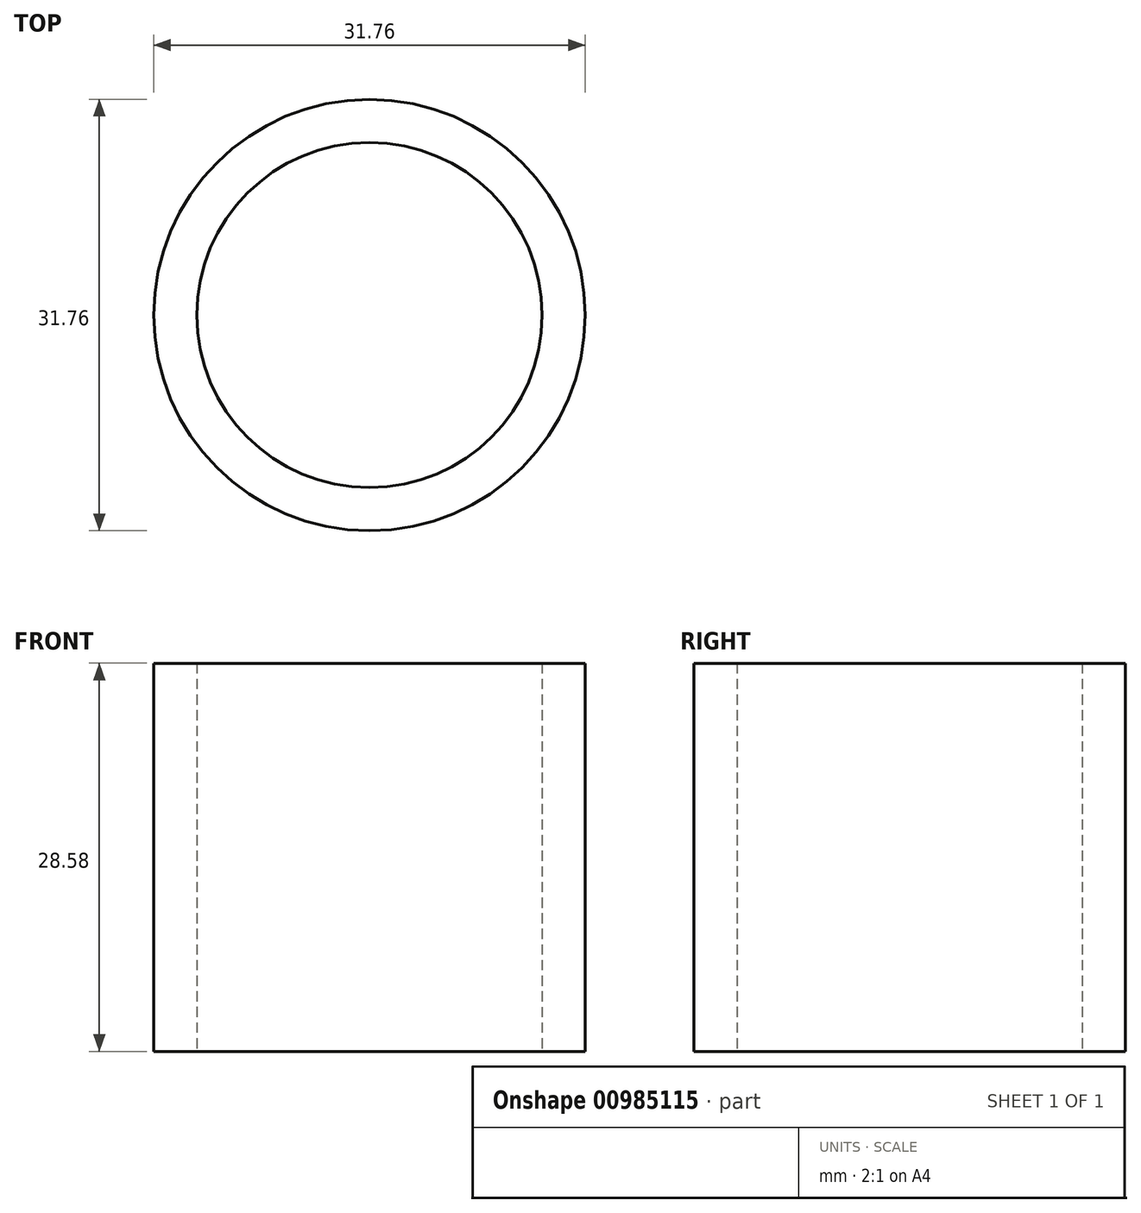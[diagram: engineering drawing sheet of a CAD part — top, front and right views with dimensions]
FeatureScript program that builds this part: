
annotation { "Feature Type Name" : "Feature", "Feature Type Description" : "" }
export const myFeature = defineFeature(function(context is Context, id is Id, definition is map)
    precondition{}
    {
        {
            var Q0;
            Q0=qCreatedBy(makeId("Top.planeOp"),FACE);
            var sketch = newSketch(context, id + "F0", { "sketchPlane" : qUnion([Q0])});
            skCircle(sketch, "E0", {"center": v(0, 0) * mm, "radius": 12.7 * mm});
            skCircle(sketch, "E1.0", {"center": v(0, 0) * mm, "radius": 15.88 * mm});
            skSolve(sketch);
        }
        {
            var Q0;
            Q0=makeQuery(id+"F0.imprint","IMPRINT",FACE,{"disambiguationData":[TD([[makeQuery(id+"F0.imprint","IMPRINT",EDGE,{"derivedFrom":sQuery(id+"F0.wireOp",EDGE,"E0")}),-1.0]])]});
            extrude(context, id + "F1", {"entities" : qUnion([Q0]), "depth" : 28.57 * mm, "offsetDistance" : 25.4 * mm});
        }
    });
